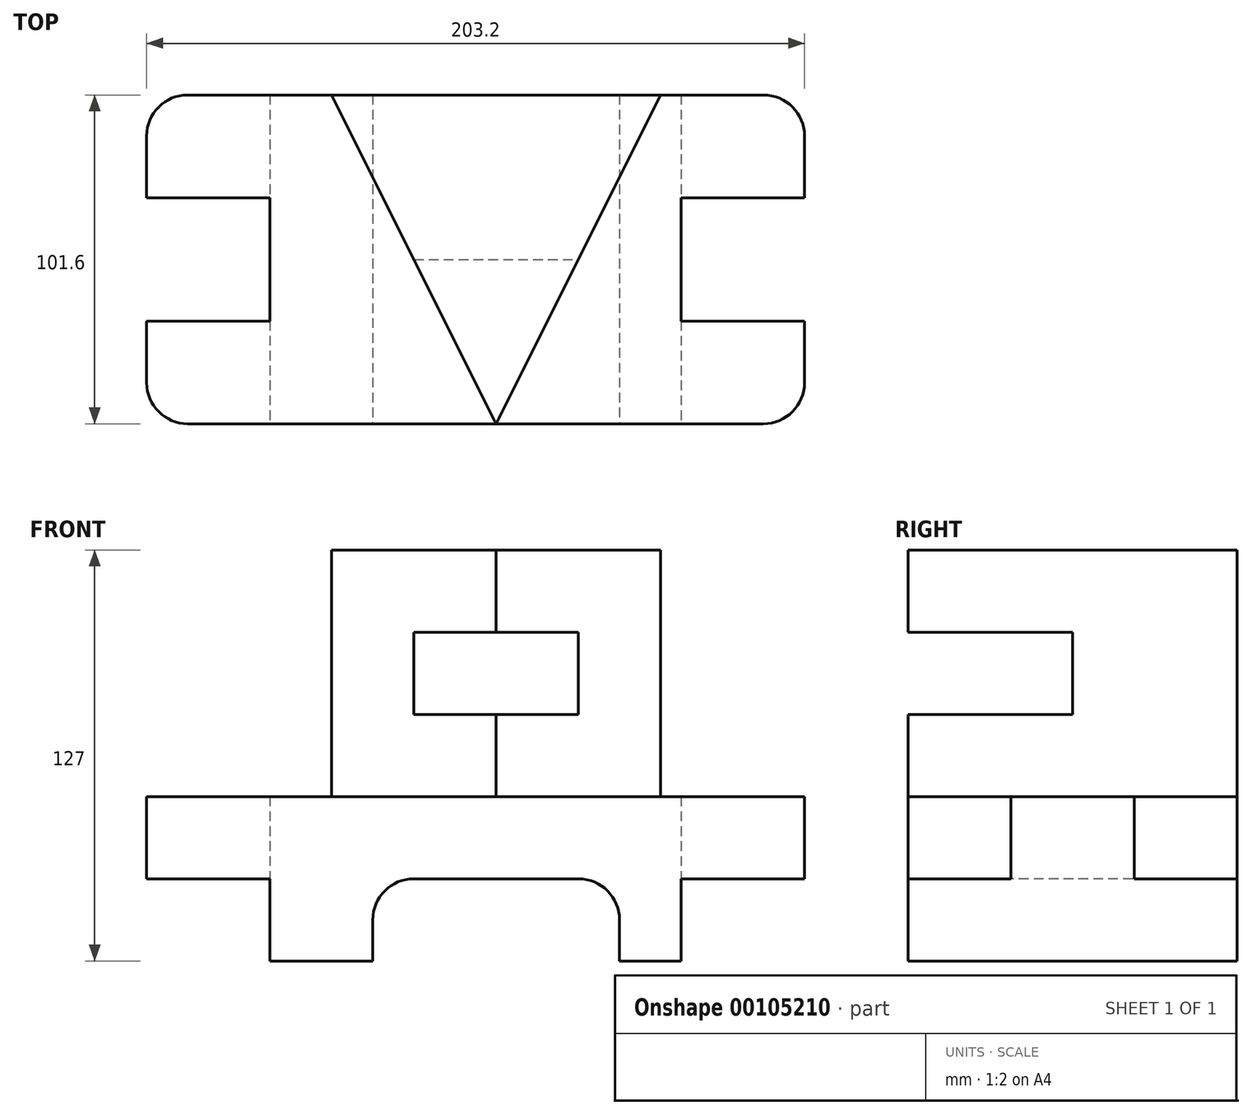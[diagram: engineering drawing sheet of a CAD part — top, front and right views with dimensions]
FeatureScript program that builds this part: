
annotation { "Feature Type Name" : "Feature", "Feature Type Description" : "" }
export const myFeature = defineFeature(function(context is Context, id is Id, definition is map)
    precondition{}
    {
        {
            var Q0;
            Q0=qCreatedBy(makeId("Top.planeOp"),FACE);
            var sketch = newSketch(context, id + "F0", { "sketchPlane" : qUnion([Q0])});
            skLineSegment(sketch, "E0", {"start": v(-107.96, 35.67) * mm, "end": v(-107.96, 54.72) * mm});
            skLineSegment(sketch, "E1", {"start": v(-107.96, 35.67) * mm, "end": v(-69.86, 35.67) * mm});
            skLineSegment(sketch, "E2", {"start": v(-69.86, 35.67) * mm, "end": v(-69.86, -2.43) * mm});
            skLineSegment(sketch, "E3", {"start": v(-69.86, -2.43) * mm, "end": v(-107.96, -2.43) * mm});
            skLineSegment(sketch, "E4", {"start": v(-107.96, -2.43) * mm, "end": v(-107.96, -21.48) * mm});
            skLineSegment(sketch, "E5", {"start": v(-95.26, -34.18) * mm, "end": v(82.54, -34.18) * mm});
            skLineSegment(sketch, "E6", {"start": v(-95.26, 67.42) * mm, "end": v(82.54, 67.42) * mm});
            skLineSegment(sketch, "E7", {"start": v(95.24, 54.72) * mm, "end": v(95.24, 35.67) * mm});
            skLineSegment(sketch, "E8", {"start": v(95.24, 35.67) * mm, "end": v(57.14, 35.67) * mm});
            skLineSegment(sketch, "E9", {"start": v(57.14, 35.67) * mm, "end": v(57.14, -2.43) * mm});
            skLineSegment(sketch, "E10", {"start": v(57.14, -2.43) * mm, "end": v(95.24, -2.43) * mm});
            skLineSegment(sketch, "E11", {"start": v(95.24, -2.43) * mm, "end": v(95.24, -21.48) * mm});
            skArc(sketch, "E12", {"start": v(-95.26, 67.42) * mm, "mid": v(-104.24, 63.7) * mm, "end": v(-107.96, 54.72) * mm});
            skArc(sketch, "E13", {"start": v(-107.96, -21.48) * mm, "mid": v(-104.24, -30.46) * mm, "end": v(-95.26, -34.18) * mm});
            skArc(sketch, "E14", {"start": v(95.24, 54.72) * mm, "mid": v(91.52, 63.7) * mm, "end": v(82.54, 67.42) * mm});
            skArc(sketch, "E15", {"start": v(82.54, -34.18) * mm, "mid": v(91.52, -30.46) * mm, "end": v(95.24, -21.48) * mm});
            skSolve(sketch);
        }
        {
            var Q0;
            Q0=makeQuery(id+"F0.imprint","IMPRINT",FACE,{"disambiguationData":[TD([[makeQuery(id+"F0.imprint","IMPRINT",EDGE,{"derivedFrom":sQuery(id+"F0.wireOp",EDGE,"E0")}),-1.0]])]});
            extrude(context, id + "F1", {"entities" : qUnion([Q0]), "depth" : 50.8 * mm});
        }
        {
            var Q0;
            Q0=makeQuery(id+"F1.opExtrude","CAP_FACE",FACE,{"disambiguationData":[OSD([sQuery(id+"F0.wireOp",EDGE,"E0"),sQuery(id+"F0.wireOp",EDGE,"E1"),sQuery(id+"F0.wireOp",EDGE,"E2"),sQuery(id+"F0.wireOp",EDGE,"E3"),sQuery(id+"F0.wireOp",EDGE,"E4"),sQuery(id+"F0.wireOp",EDGE,"E5"),sQuery(id+"F0.wireOp",EDGE,"E6"),sQuery(id+"F0.wireOp",EDGE,"E7"),sQuery(id+"F0.wireOp",EDGE,"E8"),sQuery(id+"F0.wireOp",EDGE,"E9"),sQuery(id+"F0.wireOp",EDGE,"E10"),sQuery(id+"F0.wireOp",EDGE,"E11"),sQuery(id+"F0.wireOp",EDGE,"E12"),sQuery(id+"F0.wireOp",EDGE,"E13"),sQuery(id+"F0.wireOp",EDGE,"E14"),sQuery(id+"F0.wireOp",EDGE,"E15")])],"isStart":false});
            var sketch = newSketch(context, id + "F2", { "sketchPlane" : qUnion([Q0])});
            skLineSegment(sketch, "E16", {"start": v(0, -34.18) * mm, "end": v(-50.8, 67.42) * mm});
            skLineSegment(sketch, "E17", {"start": v(-50.8, 67.42) * mm, "end": v(50.8, 67.42) * mm});
            skLineSegment(sketch, "E18", {"start": v(50.8, 67.42) * mm, "end": v(0, -34.18) * mm});
            skSolve(sketch);
        }
        {
            var Q0;
            Q0=makeQuery(id+"F2.imprint","IMPRINT",FACE,{"disambiguationData":[TD([[makeQuery(id+"F2.imprint","IMPRINT",EDGE,{"derivedFrom":sQuery(id+"F2.wireOp",EDGE,"E16")}),-1.0]])]});
            extrude(context, id + "F3", {"entities" : qUnion([Q0]), "operationType" : NewBodyOperationType.ADD, "depth" : 76.2 * mm});
        }
        {
            var Q0;
            Q0=makeQuery(id+"F1.opExtrude","SWEPT_FACE",FACE,{"disambiguationData":[OSD([sQuery(id+"F0.wireOp",EDGE,"E5")])]});
            var sketch = newSketch(context, id + "F4", { "sketchPlane" : qUnion([Q0])});
            skLineSegment(sketch, "E19.bottom", {"start": v(-25.4, 101.6) * mm, "end": v(25.4, 101.6) * mm});
            skLineSegment(sketch, "E19.top", {"start": v(-25.4, 76.2) * mm, "end": v(25.4, 76.2) * mm});
            skLineSegment(sketch, "E19.left", {"start": v(-25.4, 101.6) * mm, "end": v(-25.4, 76.2) * mm});
            skLineSegment(sketch, "E19.right", {"start": v(25.4, 101.6) * mm, "end": v(25.4, 76.2) * mm});
            skLineSegment(sketch, "E20", {"start": v(0, 101.6) * mm, "end": v(-25.4, 101.6) * mm});
            skLineSegment(sketch, "E21", {"start": v(0, 101.6) * mm, "end": v(25.4, 101.6) * mm});
            skSolve(sketch);
        }
        {
            var Q0;
            Q0 = qSketchRegion(id + "F4", true);
            extrude(context, id + "F5", {"entities" : qUnion([Q0]), "operationType" : NewBodyOperationType.REMOVE, "oppositeDirection" : true, "depth" : 50.8 * mm});
        }
        {
            var Q0;
            Q0=makeQuery(id+"F1.opExtrude","SWEPT_FACE",FACE,{"disambiguationData":[OSD([sQuery(id+"F0.wireOp",EDGE,"E5")])]});
            var sketch = newSketch(context, id + "F6", { "sketchPlane" : qUnion([Q0])});
            skLineSegment(sketch, "E22", {"start": v(-38.1, 0) * mm, "end": v(38.1, 0) * mm});
            skLineSegment(sketch, "E23", {"start": v(0, 0) * mm, "end": v(0, 25.4) * mm});
            skArc(sketch, "E24", {"start": v(-25.4, 25.4) * mm, "mid": v(-34.38, 21.68) * mm, "end": v(-38.1, 12.7) * mm});
            skArc(sketch, "E25", {"start": v(38.1, 12.7) * mm, "mid": v(34.38, 21.68) * mm, "end": v(25.4, 25.4) * mm});
            skLineSegment(sketch, "E26", {"start": v(-38.1, 12.7) * mm, "end": v(-38.1, 0) * mm});
            skLineSegment(sketch, "E27", {"start": v(-25.4, 25.4) * mm, "end": v(0, 25.4) * mm});
            skLineSegment(sketch, "E28", {"start": v(0, 25.4) * mm, "end": v(25.4, 25.4) * mm});
            skLineSegment(sketch, "E29", {"start": v(38.1, 12.7) * mm, "end": v(38.1, 0) * mm});
            skSolve(sketch);
        }
        {
            var Q0;
            {var subQ2=sQuery(id+"F6.wireOp",EDGE,"E23");Q0=makeQuery(id+"F6.imprint","IMPRINT",FACE,{"disambiguationData":[TD([[makeQuery(id+"F6.imprint","IMPRINT",EDGE,{"derivedFrom":subQ2}),1.0]])]});}
            var Q1;
            {var subQ0=sQuery(id+"F6.wireOp",EDGE,"E23");Q1=makeQuery(id+"F6.imprint","IMPRINT",FACE,{"disambiguationData":[TD([[makeQuery(id+"F6.imprint","IMPRINT",EDGE,{"derivedFrom":subQ0}),-1.0]])]});}
            extrude(context, id + "F7", {"entities" : qUnion([Q0, Q1]), "operationType" : NewBodyOperationType.REMOVE, "endBound" : BoundingType.THROUGH_ALL, "oppositeDirection" : true, "depth" : 25.4 * mm});
        }
        {
            var Q0;
            Q0=makeQuery(id+"F1.opExtrude","SWEPT_FACE",FACE,{"disambiguationData":[OSD([sQuery(id+"F0.wireOp",EDGE,"E5")])]});
            var sketch = newSketch(context, id + "F8", { "sketchPlane" : qUnion([Q0])});
            skLineSegment(sketch, "E30.bottom", {"start": v(-69.86, 25.4) * mm, "end": v(-107.96, 25.4) * mm});
            skLineSegment(sketch, "E30.top", {"start": v(-69.86, 0) * mm, "end": v(-107.96, 0) * mm});
            skLineSegment(sketch, "E30.left", {"start": v(-69.86, 25.4) * mm, "end": v(-69.86, 0) * mm});
            skLineSegment(sketch, "E30.right", {"start": v(-107.96, 25.4) * mm, "end": v(-107.96, 0) * mm});
            skSolve(sketch);
        }
        {
            var Q0;
            {var subQ0=sQuery(id+"F8.wireOp",EDGE,"E30.left");Q0=makeQuery(id+"F8.imprint","IMPRINT",FACE,{"disambiguationData":[TD([[makeQuery(id+"F8.imprint","IMPRINT",EDGE,{"derivedFrom":subQ0}),-1.0]])]});}
            var Q1;
            {var subQ0=sQuery(id+"F8.wireOp",EDGE,"E30.right");Q1=makeQuery(id+"F8.imprint","IMPRINT",FACE,{"disambiguationData":[TD([[makeQuery(id+"F8.imprint","IMPRINT",EDGE,{"derivedFrom":subQ0}),1.0]])]});}
            extrude(context, id + "F9", {"entities" : qUnion([Q0, Q1]), "operationType" : NewBodyOperationType.REMOVE, "endBound" : BoundingType.THROUGH_ALL, "oppositeDirection" : true, "depth" : 25.4 * mm});
        }
        {
            var Q0;
            Q0=makeQuery(id+"F1.opExtrude","SWEPT_FACE",FACE,{"disambiguationData":[OSD([sQuery(id+"F0.wireOp",EDGE,"E5")])]});
            var sketch = newSketch(context, id + "F10", { "sketchPlane" : qUnion([Q0])});
            skLineSegment(sketch, "E31.bottom", {"start": v(57.14, 0) * mm, "end": v(95.24, 0) * mm});
            skLineSegment(sketch, "E31.top", {"start": v(57.14, 25.4) * mm, "end": v(95.24, 25.4) * mm});
            skLineSegment(sketch, "E31.left", {"start": v(57.14, 0) * mm, "end": v(57.14, 25.4) * mm});
            skLineSegment(sketch, "E31.right", {"start": v(95.24, 0) * mm, "end": v(95.24, 25.4) * mm});
            skSolve(sketch);
        }
        {
            var Q0;
            {var subQ3=sQuery(id+"F10.wireOp",EDGE,"E31.right");Q0=makeQuery(id+"F10.imprint","IMPRINT",FACE,{"disambiguationData":[TD([[makeQuery(id+"F10.imprint","IMPRINT",EDGE,{"derivedFrom":subQ3}),1.0]])]});}
            var Q1;
            {var subQ5=sQuery(id+"F10.wireOp",EDGE,"E31.left");Q1=makeQuery(id+"F10.imprint","IMPRINT",FACE,{"disambiguationData":[TD([[makeQuery(id+"F10.imprint","IMPRINT",EDGE,{"derivedFrom":subQ5}),-1.0]])]});}
            extrude(context, id + "F11", {"entities" : qUnion([Q0, Q1]), "operationType" : NewBodyOperationType.REMOVE, "endBound" : BoundingType.THROUGH_ALL, "oppositeDirection" : true, "depth" : 25.4 * mm});
        }
    });
